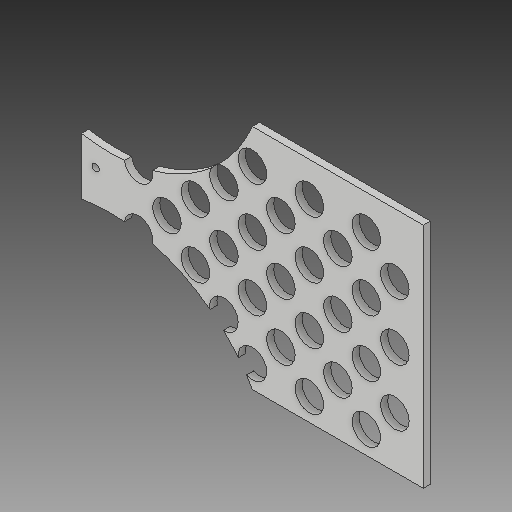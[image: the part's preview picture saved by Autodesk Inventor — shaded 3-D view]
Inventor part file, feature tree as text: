
AUTODESK INVENTOR PART (.ipt)
format: ipt  version: 2017 (Build 210142000, 142)  size: 259,072 bytes
history: native  units: in
note: dims shown in document units (in); Inventor stores cm internally (conversion verified against a paired STEP export)
features: sketch x4, extrude x2, hole x2, projected_geometry x1
ambient origin geometry x8: Origin, YZ Plane, XZ Plane, XY Plane, X Axis, Y Axis, Z Axis, Center Point
bodies: Solid1 (feature_tree)
feature tree (9):
  extrude  "Extrusion1"  Depth=4.0in
  hole  "Hole1"  [1 undecoded]
  hole  "Hole2"  [1 undecoded]
  extrude  "Extrusion2"  Depth=0.25in
  sketch  "Sketch1"  dims[d0=6.0in d1=4.0in]
  sketch  "Sketch2"  dims[d2=0.125in d3=0.0in d5=1.0in]
  sketch  "Sketch3"  dims[d6=1.9685in d8=1.0in d9=1.5748in d11=1.0in d14=1.9685in d16=1.0in d17=1.1811in d19=1.0in]
  sketch  "Sketch4"  dims[d22=0.5in d23=0.75in d24=0.375in d25=0.25in d26=0.5635in d27=1.0in d28=0.8108in d29=0.25in d30=0.125in d31=0.75in d32=0.375in d33=0.25in d34=0.5635in d35=1.0in d36=0.8108in d37=1.0in d38=0.0in d39=4.0in]
  projected_geometry  "Projected Loop1"
note: 2 required parameter values undecoded (feature->parameter linkage not recoverable at this tier; creation-order binding heuristic only, values carry confidence <= 0.55)
